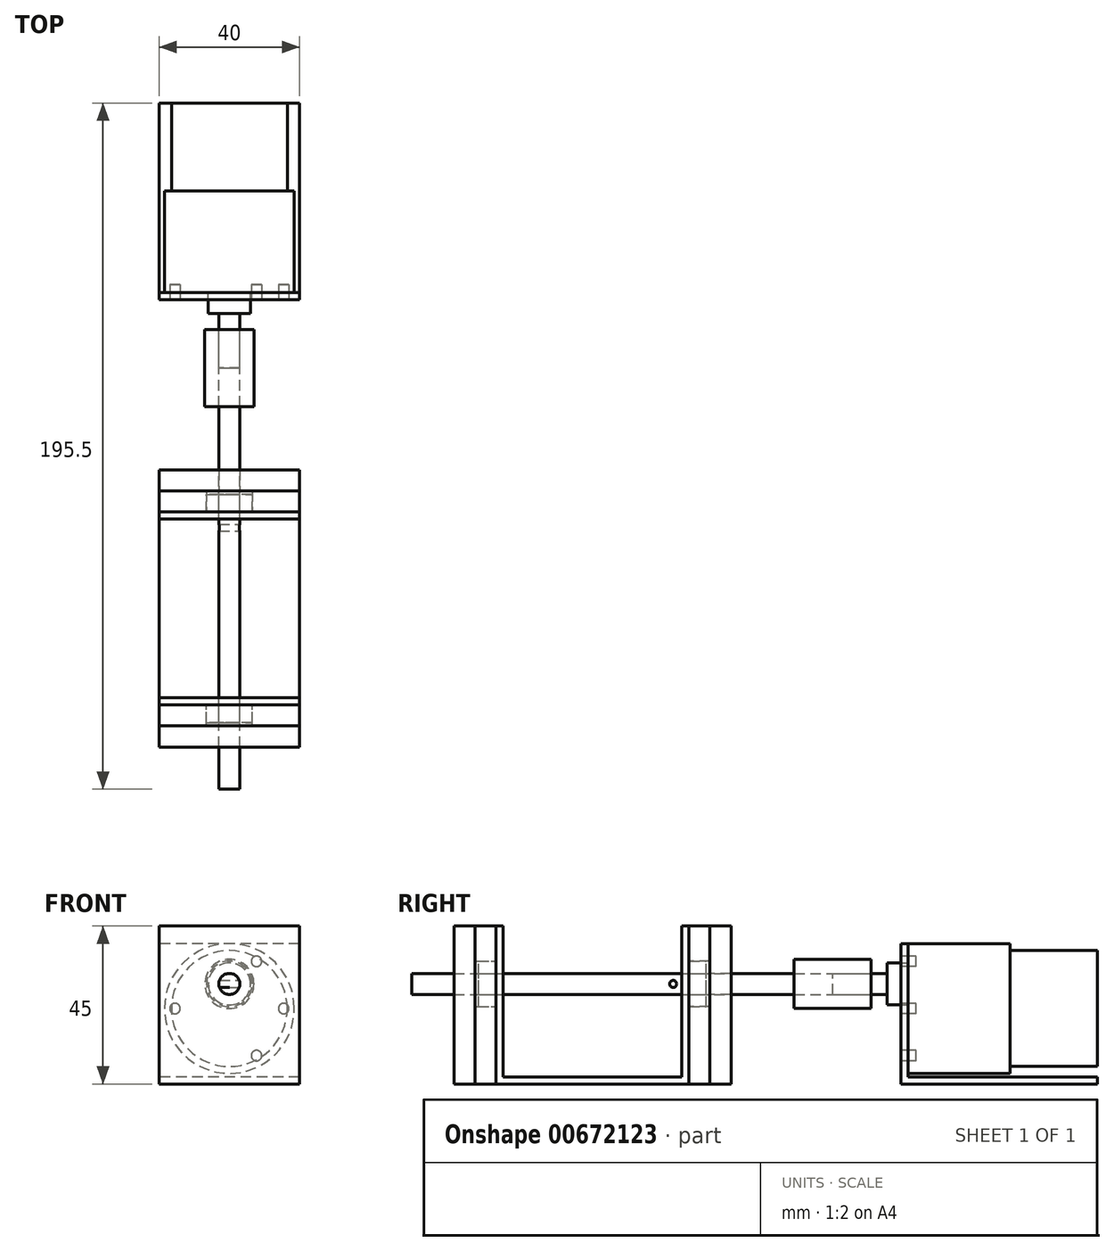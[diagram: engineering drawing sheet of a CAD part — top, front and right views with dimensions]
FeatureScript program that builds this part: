
annotation { "Feature Type Name" : "Feature", "Feature Type Description" : "" }
export const myFeature = defineFeature(function(context is Context, id is Id, definition is map)
    precondition{}
    {
        {
            var Q0;
            Q0=qCreatedBy(makeId("Front.planeOp"),FACE);
            var sketch = newSketch(context, id + "F0", { "sketchPlane" : qUnion([Q0])});
            skCircle(sketch, "E0", {"center": v(0, 0) * mm, "radius": 16.5 * mm});
            skSolve(sketch);
        }
        {
            var Q0;
            Q0=makeQuery(id+"F0.imprint","IMPRINT",FACE,{"disambiguationData":[TD([[makeQuery(id+"F0.imprint","IMPRINT",EDGE,{"derivedFrom":sQuery(id+"F0.wireOp",EDGE,"E0")}),1.0]])]});
            extrude(context, id + "F1", {"entities" : qUnion([Q0]), "depth" : 25 * mm, "offsetDistance" : 25 * mm});
        }
        {
            var Q0;
            Q0=makeQuery(id+"F1.opExtrude","CAP_FACE",FACE,{"disambiguationData":[OSD([sQuery(id+"F0.wireOp",EDGE,"E0")])],"isStart":false});
            var sketch = newSketch(context, id + "F2", { "sketchPlane" : qUnion([Q0])});
            skCircle(sketch, "E1", {"center": v(0, 0) * mm, "radius": 18.5 * mm});
            skSolve(sketch);
        }
        {
            var Q0;
            Q0 = qSketchRegion(id + "F2", true);
            extrude(context, id + "F3", {"entities" : qUnion([Q0]), "operationType" : NewBodyOperationType.ADD, "depth" : 29 * mm, "offsetDistance" : 25 * mm});
        }
        {
            var Q0;
            Q0=makeQuery(id+"F3.opExtrude","CAP_FACE",FACE,{"disambiguationData":[OSD([sQuery(id+"F2.wireOp",EDGE,"E1")])],"isStart":false});
            var sketch = newSketch(context, id + "F4", { "sketchPlane" : qUnion([Q0])});
            skCircle(sketch, "E2", {"center": v(0, 7) * mm, "radius": 6 * mm});
            skSolve(sketch);
        }
        {
            var Q0;
            Q0 = qSketchRegion(id + "F4", true);
            extrude(context, id + "F5", {"entities" : qUnion([Q0]), "operationType" : NewBodyOperationType.ADD, "depth" : 6 * mm, "offsetDistance" : 25 * mm});
        }
        {
            var Q0;
            Q0=makeQuery(id+"F5.opExtrude","CAP_FACE",FACE,{"disambiguationData":[OSD([sQuery(id+"F4.wireOp",EDGE,"E2")])],"isStart":false});
            var sketch = newSketch(context, id + "F6", { "sketchPlane" : qUnion([Q0])});
            skCircle(sketch, "E3", {"center": v(0, 7) * mm, "radius": 3 * mm});
            skSolve(sketch);
        }
        {
            var Q0;
            Q0=makeQuery(id+"F6.imprint","IMPRINT",FACE,{"disambiguationData":[TD([[makeQuery(id+"F6.imprint","IMPRINT",EDGE,{"derivedFrom":sQuery(id+"F6.wireOp",EDGE,"E3")}),1.0]])]});
            extrude(context, id + "F7", {"entities" : qUnion([Q0]), "operationType" : NewBodyOperationType.ADD, "depth" : 15.5 * mm, "offsetDistance" : 25 * mm});
        }
        {
            var Q0;
            Q0=makeQuery(id+"F3.opExtrude","CAP_FACE",FACE,{"disambiguationData":[OSD([sQuery(id+"F2.wireOp",EDGE,"E1")])],"isStart":false});
            var sketch = newSketch(context, id + "F8", { "sketchPlane" : qUnion([Q0])});
            skCircle(sketch, "E4", {"center": v(0, 0) * mm, "radius": 15.5 * mm, "construction": true});
            skCircle(sketch, "E5", {"center": v(-15.5, 0) * mm, "radius": 1.5 * mm});
            skCircle(sketch, "E6", {"center": v(7.75, 13.42) * mm, "radius": 1.5 * mm});
            skCircle(sketch, "E7", {"center": v(15.5, 0) * mm, "radius": 1.5 * mm});
            skCircle(sketch, "E8", {"center": v(7.75, -13.42) * mm, "radius": 1.5 * mm});
            skLineSegment(sketch, "E9", {"start": v(0, 0) * mm, "end": v(7.75, 13.42) * mm, "construction": true});
            skLineSegment(sketch, "E10", {"start": v(0, 0) * mm, "end": v(7.75, -13.42) * mm, "construction": true});
            skSolve(sketch);
        }
        {
            var Q0;
            Q0=qCreatedBy(makeId("Top.planeOp"),FACE);
            cPlane(context, id + "F9", {"entities" : qUnion([Q0]), "cplaneType" : CPlaneType.OFFSET, "offset" : 18.5 * mm, "width" : 150 * mm, "height" : 150 * mm});
        }
        {
            var Q0;
            Q0=qCreatedBy(makeId("Right.planeOp"),FACE);
            var sketch = newSketch(context, id + "F10", { "sketchPlane" : qUnion([Q0])});
            skLineSegment(sketch, "E11", {"start": v(-56, 18.5) * mm, "end": v(-56, -21.5) * mm});
            skLineSegment(sketch, "E12", {"start": v(-56, -21.5) * mm, "end": v(0, -21.5) * mm});
            skLineSegment(sketch, "E13", {"start": v(0, -21.5) * mm, "end": v(0, -19.5) * mm});
            skLineSegment(sketch, "E14", {"start": v(0, -19.5) * mm, "end": v(-54, -19.5) * mm});
            skLineSegment(sketch, "E15", {"start": v(-54, -19.5) * mm, "end": v(-54, 18.5) * mm});
            skLineSegment(sketch, "E16", {"start": v(-54, 18.5) * mm, "end": v(-56, 18.5) * mm});
            skSolve(sketch);
        }
        {
            var Q0;
            Q0=makeQuery(id+"F10.imprint","IMPRINT",FACE,{"disambiguationData":[TD([[makeQuery(id+"F10.imprint","IMPRINT",EDGE,{"derivedFrom":sQuery(id+"F10.wireOp",EDGE,"E11")}),1.0]])]});
            extrude(context, id + "F11", {"entities" : qUnion([Q0]), "endBound" : BoundingType.SYMMETRIC, "depth" : 40 * mm, "offsetDistance" : 25 * mm});
        }
        {
            var Q0;
            Q0 = qSketchRegion(id + "F8", true);
            extrude(context, id + "F12", {"entities" : qUnion([Q0]), "operationType" : NewBodyOperationType.REMOVE, "endBound" : BoundingType.SYMMETRIC, "oppositeDirection" : true, "depth" : 4.5 * mm, "offsetDistance" : 25 * mm});
        }
        {
            var Q0;
            Q0=makeQuery(id+"F1.opExtrude","SWEPT_BODY",BODY,{"disambiguationData":[OSD([sQuery(id+"F0.wireOp",EDGE,"E0")])]});
            var Q1;
            Q1=makeQuery(id+"F11.opExtrude","SWEPT_BODY",BODY,{"disambiguationData":[OSD([sQuery(id+"F10.wireOp",EDGE,"E11"),sQuery(id+"F10.wireOp",EDGE,"E12"),sQuery(id+"F10.wireOp",EDGE,"E13"),sQuery(id+"F10.wireOp",EDGE,"E14"),sQuery(id+"F10.wireOp",EDGE,"E15"),sQuery(id+"F10.wireOp",EDGE,"E16")])]});
            booleanBodies(context, id + "F13", {"operationType" : BooleanOperationType.SUBTRACTION, "tools" : qUnion([Q0]), "targets" : qUnion([Q1]), "keepTools" : true});
        }
        {
            var Q0;
            Q0=makeQuery(id+"F7.opExtrude","CAP_FACE",FACE,{"disambiguationData":[OSD([sQuery(id+"F6.wireOp",EDGE,"E3")])],"isStart":false});
            cPlane(context, id + "F14", {"entities" : qUnion([Q0]), "cplaneType" : CPlaneType.OFFSET, "offset" : 11 * mm, "oppositeDirection" : true, "width" : 150 * mm, "height" : 150 * mm});
        }
        {
            var Q0;
            Q0=qCreatedBy(id+"F14.planeOp",FACE);
            var sketch = newSketch(context, id + "F15", { "sketchPlane" : qUnion([Q0])});
            skCircle(sketch, "E17", {"center": v(0, 7) * mm, "radius": 7 * mm});
            skCircle(sketch, "E18", {"center": v(0, 7) * mm, "radius": 3 * mm});
            skSolve(sketch);
        }
        {
            var Q0;
            Q0 = qSketchRegion(id + "F15", true);
            extrude(context, id + "F16", {"entities" : qUnion([Q0]), "depth" : 22 * mm, "offsetDistance" : 25 * mm});
        }
        {
            var Q0;
            Q0=makeQuery(id+"F7.opExtrude","CAP_FACE",FACE,{"disambiguationData":[OSD([sQuery(id+"F6.wireOp",EDGE,"E3")])],"isStart":false});
            var sketch = newSketch(context, id + "F17", { "sketchPlane" : qUnion([Q0])});
            skCircle(sketch, "E19", {"center": v(0, 7) * mm, "radius": 3 * mm});
            skSolve(sketch);
        }
        {
            var Q0;
            Q0 = qSketchRegion(id + "F17", true);
            extrude(context, id + "F18", {"entities" : qUnion([Q0]), "depth" : 120 * mm, "offsetDistance" : 25 * mm});
        }
        {
            var Q0;
            Q0=makeQuery(id+"F16.opExtrude","CAP_FACE",FACE,{"disambiguationData":[OSD([sQuery(id+"F15.wireOp",EDGE,"E17"),sQuery(id+"F15.wireOp",EDGE,"E18")])],"isStart":false});
            cPlane(context, id + "F19", {"entities" : qUnion([Q0]), "cplaneType" : CPlaneType.OFFSET, "offset" : 25 * mm, "width" : 150 * mm, "height" : 150 * mm});
        }
        {
            var Q0;
            Q0=qCreatedBy(id+"F19.planeOp",FACE);
            var sketch = newSketch(context, id + "F20", { "sketchPlane" : qUnion([Q0])});
            skCircle(sketch, "E20", {"center": v(0, 7) * mm, "radius": 6.5 * mm});
            skSolve(sketch);
        }
        {
            var Q0;
            Q0 = qSketchRegion(id + "F20", true);
            extrude(context, id + "F21", {"entities" : qUnion([Q0]), "depth" : 5 * mm, "offsetDistance" : 25 * mm});
        }
        {
            var Q0;
            Q0=makeQuery(id+"F21.opExtrude","SWEPT_BODY",BODY,{"disambiguationData":[OSD([sQuery(id+"F20.wireOp",EDGE,"E20")])]});
            transform(context, id + "F22", {"entities" : qUnion([Q0]), "transformType" : TransformType.TRANSLATION_3D, "dx" : 0 * mm, "dy" : -60 * mm, "dz" : 0 * mm, "makeCopy" : true});
        }
        {
            var Q0;
            Q0=qCreatedBy(makeId("Right.planeOp"),FACE);
            var sketch = newSketch(context, id + "F23", { "sketchPlane" : qUnion([Q0])});
            skLineSegment(sketch, "E21", {"start": v(-169.5, 23.5) * mm, "end": v(-169.5, -19.5) * mm});
            skLineSegment(sketch, "E22", {"start": v(-169.5, -19.5) * mm, "end": v(-118.5, -19.5) * mm});
            skLineSegment(sketch, "E23", {"start": v(-118.5, -19.5) * mm, "end": v(-118.5, 23.5) * mm});
            skLineSegment(sketch, "E24", {"start": v(-118.5, 23.5) * mm, "end": v(-116.5, 23.5) * mm});
            skLineSegment(sketch, "E25", {"start": v(-116.5, 23.5) * mm, "end": v(-116.5, -21.5) * mm});
            skLineSegment(sketch, "E26", {"start": v(-116.5, -21.5) * mm, "end": v(-171.5, -21.5) * mm});
            skLineSegment(sketch, "E27", {"start": v(-171.5, -21.5) * mm, "end": v(-171.5, 23.5) * mm});
            skLineSegment(sketch, "E28", {"start": v(-171.5, 23.5) * mm, "end": v(-169.5, 23.5) * mm});
            skSolve(sketch);
        }
        {
            var Q0;
            Q0 = qSketchRegion(id + "F23", true);
            extrude(context, id + "F24", {"entities" : qUnion([Q0]), "endBound" : BoundingType.SYMMETRIC, "oppositeDirection" : true, "depth" : 40 * mm, "offsetDistance" : 25 * mm});
        }
        {
            var Q0;
            Q0=makeQuery(id+"F18.opExtrude","SWEPT_BODY",BODY,{"disambiguationData":[OSD([sQuery(id+"F17.wireOp",EDGE,"E19")])]});
            var Q1;
            Q1=makeQuery(id+"F24.opExtrude","SWEPT_BODY",BODY,{"disambiguationData":[OSD([sQuery(id+"F23.wireOp",EDGE,"E21"),sQuery(id+"F23.wireOp",EDGE,"E22"),sQuery(id+"F23.wireOp",EDGE,"E23"),sQuery(id+"F23.wireOp",EDGE,"E24"),sQuery(id+"F23.wireOp",EDGE,"E25"),sQuery(id+"F23.wireOp",EDGE,"E26"),sQuery(id+"F23.wireOp",EDGE,"E27"),sQuery(id+"F23.wireOp",EDGE,"E28")])]});
            var Q2;
            Q2=makeQuery(id+"F21.opExtrude","SWEPT_BODY",BODY,{"disambiguationData":[OSD([sQuery(id+"F20.wireOp",EDGE,"E20")])]});
            var Q3;
            Q3=makeQuery(id+"F22.opPattern","COPY",BODY,{"derivedFrom":makeQuery(id+"F21.opExtrude","SWEPT_BODY",BODY,{"disambiguationData":[OSD([sQuery(id+"F20.wireOp",EDGE,"E20")])]}),"instanceName":"1"});
            booleanBodies(context, id + "F25", {"operationType" : BooleanOperationType.SUBTRACTION, "tools" : qUnion([Q0]), "targets" : qUnion([Q1, Q2, Q3]), "keepTools" : true});
        }
        {
            var Q0;
            Q0=makeQuery(id+"F24.opExtrude","SWEPT_FACE",FACE,{"disambiguationData":[OSD([sQuery(id+"F23.wireOp",EDGE,"E27")])]});
            var sketch = newSketch(context, id + "F26", { "sketchPlane" : qUnion([Q0])});
            skLineSegment(sketch, "E29", {"start": v(-20, 23.5) * mm, "end": v(20, 23.5) * mm});
            skLineSegment(sketch, "E30", {"start": v(20, 23.5) * mm, "end": v(20, -21.5) * mm});
            skLineSegment(sketch, "E31", {"start": v(20, -21.5) * mm, "end": v(-20, -21.5) * mm});
            skLineSegment(sketch, "E32", {"start": v(-20, -21.5) * mm, "end": v(-20, 23.5) * mm});
            skCircle(sketch, "E33", {"center": v(0, 7) * mm, "radius": 6.5 * mm});
            skSolve(sketch);
        }
        {
            var Q0;
            Q0 = qSketchRegion(id + "F26", true);
            extrude(context, id + "F27", {"entities" : qUnion([Q0]), "depth" : 6 * mm, "offsetDistance" : 25 * mm});
        }
        {
            var Q0;
            Q0=makeQuery(id+"F27.opExtrude","CAP_FACE",FACE,{"disambiguationData":[OSD([sQuery(id+"F26.wireOp",EDGE,"E29"),sQuery(id+"F26.wireOp",EDGE,"E30"),sQuery(id+"F26.wireOp",EDGE,"E31"),sQuery(id+"F26.wireOp",EDGE,"E32"),sQuery(id+"F26.wireOp",EDGE,"E33")])],"isStart":false});
            var sketch = newSketch(context, id + "F28", { "sketchPlane" : qUnion([Q0])});
            skLineSegment(sketch, "E34.bottom", {"start": v(-20, 23.5) * mm, "end": v(20, 23.5) * mm});
            skLineSegment(sketch, "E34.top", {"start": v(-20, -21.5) * mm, "end": v(20, -21.5) * mm});
            skLineSegment(sketch, "E34.left", {"start": v(-20, 23.5) * mm, "end": v(-20, -21.5) * mm});
            skLineSegment(sketch, "E34.right", {"start": v(20, 23.5) * mm, "end": v(20, -21.5) * mm});
            skCircle(sketch, "E35", {"center": v(0, 7) * mm, "radius": 3 * mm});
            skSolve(sketch);
        }
        {
            var Q0;
            Q0 = qSketchRegion(id + "F28", true);
            extrude(context, id + "F29", {"entities" : qUnion([Q0]), "depth" : 6 * mm, "offsetDistance" : 25 * mm});
        }
        {
            var Q0;
            Q0=makeQuery(id+"F24.opExtrude","SWEPT_FACE",FACE,{"disambiguationData":[OSD([sQuery(id+"F23.wireOp",EDGE,"E25")])]});
            var sketch = newSketch(context, id + "F30", { "sketchPlane" : qUnion([Q0])});
            skCircle(sketch, "E36", {"center": v(0, 7) * mm, "radius": 6.5 * mm});
            skLineSegment(sketch, "E37.bottom", {"start": v(-20, 23.5) * mm, "end": v(20, 23.5) * mm});
            skLineSegment(sketch, "E37.top", {"start": v(-20, -21.5) * mm, "end": v(20, -21.5) * mm});
            skLineSegment(sketch, "E37.left", {"start": v(-20, 23.5) * mm, "end": v(-20, -21.5) * mm});
            skLineSegment(sketch, "E37.right", {"start": v(20, 23.5) * mm, "end": v(20, -21.5) * mm});
            skSolve(sketch);
        }
        {
            var Q0;
            Q0 = qSketchRegion(id + "F30", true);
            extrude(context, id + "F31", {"entities" : qUnion([Q0]), "depth" : 6 * mm, "offsetDistance" : 25 * mm});
        }
        {
            var Q0;
            Q0=makeQuery(id+"F31.opExtrude","CAP_FACE",FACE,{"disambiguationData":[OSD([sQuery(id+"F30.wireOp",EDGE,"E36"),sQuery(id+"F30.wireOp",EDGE,"E37.bottom"),sQuery(id+"F30.wireOp",EDGE,"E37.top"),sQuery(id+"F30.wireOp",EDGE,"E37.left"),sQuery(id+"F30.wireOp",EDGE,"E37.right")])],"isStart":false});
            var sketch = newSketch(context, id + "F32", { "sketchPlane" : qUnion([Q0])});
            skLineSegment(sketch, "E38.bottom", {"start": v(-20, 23.5) * mm, "end": v(20, 23.5) * mm});
            skLineSegment(sketch, "E38.top", {"start": v(-20, -21.5) * mm, "end": v(20, -21.5) * mm});
            skLineSegment(sketch, "E38.left", {"start": v(-20, 23.5) * mm, "end": v(-20, -21.5) * mm});
            skLineSegment(sketch, "E38.right", {"start": v(20, 23.5) * mm, "end": v(20, -21.5) * mm});
            skCircle(sketch, "E39", {"center": v(0, 7) * mm, "radius": 3 * mm});
            skSolve(sketch);
        }
        {
            var Q0;
            Q0 = qSketchRegion(id + "F32", true);
            extrude(context, id + "F33", {"entities" : qUnion([Q0]), "depth" : 6 * mm, "offsetDistance" : 25 * mm});
        }
        {
            var Q0;
            Q0=qCreatedBy(makeId("Right.planeOp"),FACE);
            var sketch = newSketch(context, id + "F34", { "sketchPlane" : qUnion([Q0])});
            skCircle(sketch, "E40", {"center": v(-121, 7) * mm, "radius": 1 * mm});
            skSolve(sketch);
        }
        {
            var Q0;
            Q0 = qSketchRegion(id + "F34", true);
            extrude(context, id + "F35", {"entities" : qUnion([Q0]), "operationType" : NewBodyOperationType.REMOVE, "endBound" : BoundingType.SYMMETRIC, "oppositeDirection" : true, "depth" : 25 * mm, "offsetDistance" : 25 * mm});
        }
    });
